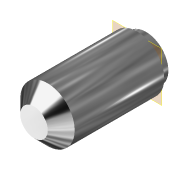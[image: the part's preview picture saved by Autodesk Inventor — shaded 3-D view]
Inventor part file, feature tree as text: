
AUTODESK INVENTOR PART (.ipt)
format: ipt  version: 2019.4 (Build 234330000, 330)  size: 103,424 bytes
history: native  units: mm
features: extrude x2, plane x1, chamfer x1, sketch x1
ambient origin geometry x8: Origin, YZ Plane, XZ Plane, XY Plane, X Axis, Y Axis, Z Axis, Center Point
bodies: Solid1 (feature_tree)
feature tree (5):
  plane  "Work Plane3"
  extrude  "Extrusion1"  Depth=4.0mm TaperAngle=45.0deg
  chamfer  "Chamfer2"  Distance=20.0mm
  extrude  "Extrusion2"  Depth=4.0mm TaperAngle=0.0deg
  sketch  "Sketch3"  dims[d1=46.0mm d2=0.0mm d6=6.0mm d7=2.0mm d8=45.0deg d9=20.0mm d10=4.0mm d11=0.0mm d12=24.3mm]
